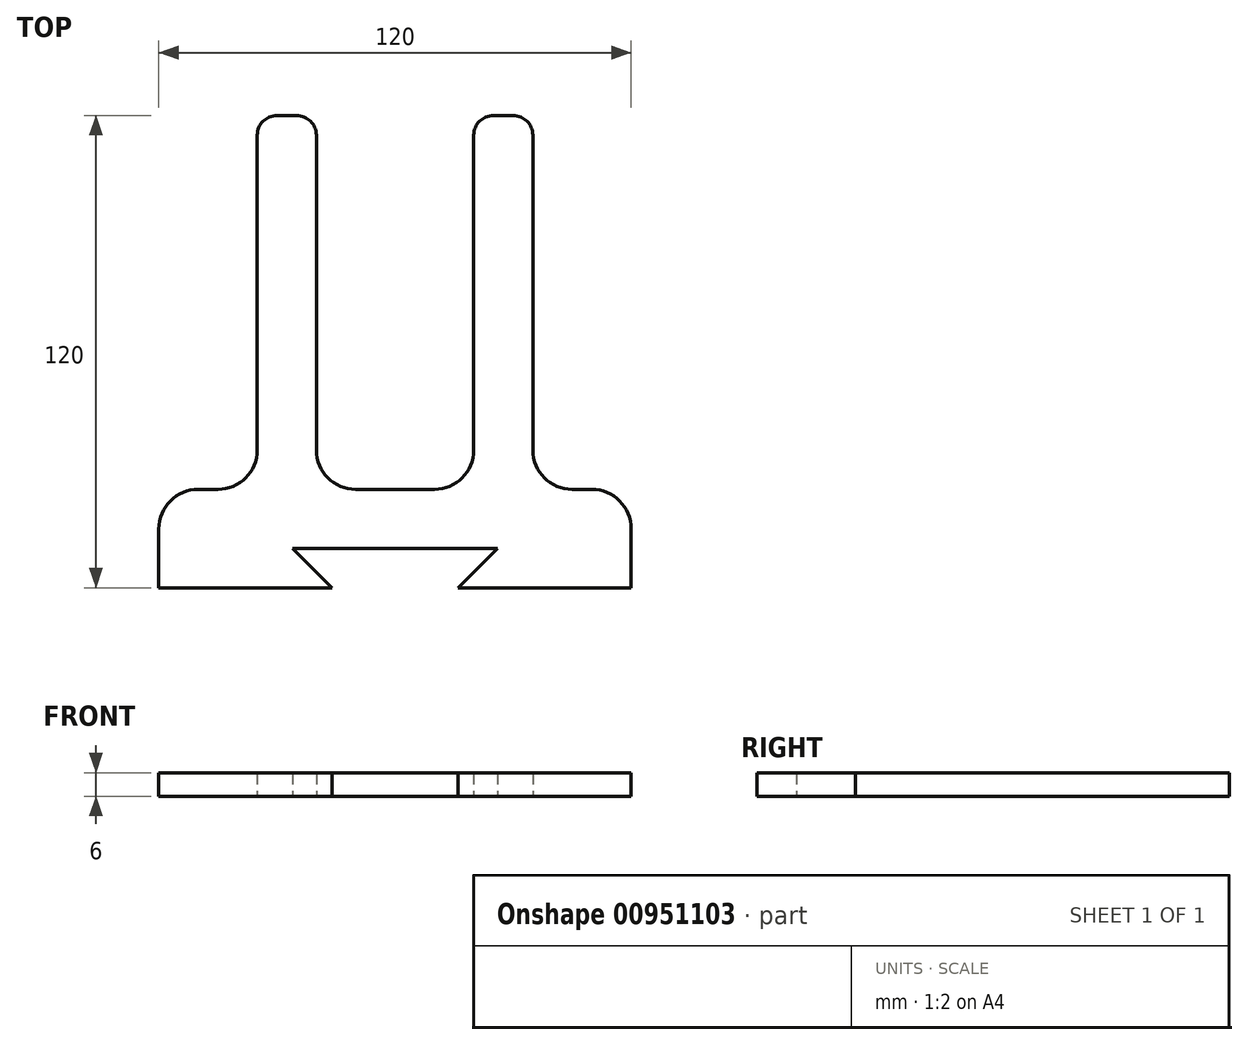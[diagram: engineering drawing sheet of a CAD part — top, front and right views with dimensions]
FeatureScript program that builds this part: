
annotation { "Feature Type Name" : "Feature", "Feature Type Description" : "" }
export const myFeature = defineFeature(function(context is Context, id is Id, definition is map)
    precondition{}
    {
        {
            var Q0;
            Q0=qCreatedBy(makeId("Top.planeOp"),FACE);
            var sketch = newSketch(context, id + "F0", { "sketchPlane" : qUnion([Q0])});
            skLineSegment(sketch, "E0", {"start": v(80, -30.9) * mm, "end": v(80, -15.9) * mm});
            skLineSegment(sketch, "E1", {"start": v(70, -5.9) * mm, "end": v(65, -5.9) * mm});
            skLineSegment(sketch, "E2", {"start": v(55, 4.1) * mm, "end": v(55, 84.1) * mm});
            skLineSegment(sketch, "E3", {"start": v(50, 89.1) * mm, "end": v(45, 89.1) * mm});
            skLineSegment(sketch, "E4", {"start": v(40, 84.1) * mm, "end": v(40, 4.1) * mm});
            skLineSegment(sketch, "E5", {"start": v(30, -5.9) * mm, "end": v(10, -5.9) * mm});
            skLineSegment(sketch, "E6", {"start": v(0, 4.1) * mm, "end": v(0, 84.1) * mm});
            skLineSegment(sketch, "E7", {"start": v(-5, 89.1) * mm, "end": v(-10, 89.1) * mm});
            skLineSegment(sketch, "E8", {"start": v(-15, 84.1) * mm, "end": v(-15, 4.1) * mm});
            skLineSegment(sketch, "E9", {"start": v(-25, -5.9) * mm, "end": v(-30, -5.9) * mm});
            skLineSegment(sketch, "E10", {"start": v(-40, -15.9) * mm, "end": v(-40, -30.9) * mm});
            skPoint(sketch, "E11.visualSharp", {"position": v(55, -5.9) * mm});
            skArc(sketch, "E11.filletArc", {"start": v(55, 4.1) * mm, "mid": v(57.93, -2.97) * mm, "end": v(65, -5.9) * mm});
            skPoint(sketch, "E12.visualSharp", {"position": v(40, -5.9) * mm});
            skArc(sketch, "E12.filletArc", {"start": v(30, -5.9) * mm, "mid": v(37.07, -2.97) * mm, "end": v(40, 4.1) * mm});
            skPoint(sketch, "E13.visualSharp", {"position": v(0, -5.9) * mm});
            skArc(sketch, "E13.filletArc", {"start": v(0, 4.1) * mm, "mid": v(2.93, -2.97) * mm, "end": v(10, -5.9) * mm});
            skPoint(sketch, "E14.visualSharp", {"position": v(-15, -5.9) * mm});
            skArc(sketch, "E14.filletArc", {"start": v(-25, -5.9) * mm, "mid": v(-17.93, -2.97) * mm, "end": v(-15, 4.1) * mm});
            skPoint(sketch, "E15.visualSharp", {"position": v(-40, -5.9) * mm});
            skArc(sketch, "E15.filletArc", {"start": v(-30, -5.9) * mm, "mid": v(-37.07, -8.82) * mm, "end": v(-40, -15.9) * mm});
            skPoint(sketch, "E16.visualSharp", {"position": v(80, -5.9) * mm});
            skArc(sketch, "E16.filletArc", {"start": v(80, -15.9) * mm, "mid": v(77.07, -8.82) * mm, "end": v(70, -5.9) * mm});
            skPoint(sketch, "E17.visualSharp", {"position": v(55, 89.1) * mm});
            skArc(sketch, "E17.filletArc", {"start": v(55, 84.1) * mm, "mid": v(53.54, 87.64) * mm, "end": v(50, 89.1) * mm});
            skPoint(sketch, "E18.visualSharp", {"position": v(40, 89.1) * mm});
            skArc(sketch, "E18.filletArc", {"start": v(45, 89.1) * mm, "mid": v(41.46, 87.64) * mm, "end": v(40, 84.1) * mm});
            skPoint(sketch, "E19.visualSharp", {"position": v(0, 89.1) * mm});
            skArc(sketch, "E19.filletArc", {"start": v(0, 84.1) * mm, "mid": v(-1.46, 87.64) * mm, "end": v(-5, 89.1) * mm});
            skPoint(sketch, "E20.visualSharp", {"position": v(-15, 89.1) * mm});
            skArc(sketch, "E20.filletArc", {"start": v(-10, 89.1) * mm, "mid": v(-13.54, 87.64) * mm, "end": v(-15, 84.1) * mm});
            skPoint(sketch, "E21.center.orphan", {"position": v(-27.5, -18.4) * mm});
            skPoint(sketch, "E22.end.orphan", {"position": v(0, -30.9) * mm});
            skLineSegment(sketch, "E23", {"start": v(-40, -30.9) * mm, "end": v(4, -30.9) * mm});
            skLineSegment(sketch, "E24", {"start": v(80, -30.9) * mm, "end": v(36, -30.9) * mm});
            skLineSegment(sketch, "E25", {"start": v(36, -30.9) * mm, "end": v(46, -20.9) * mm});
            skLineSegment(sketch, "E26", {"start": v(4, -30.9) * mm, "end": v(-6, -20.9) * mm});
            skLineSegment(sketch, "E27", {"start": v(20, -20.9) * mm, "end": v(-6, -20.9) * mm});
            skLineSegment(sketch, "E28", {"start": v(-6, -20.9) * mm, "end": v(46, -20.9) * mm});
            skPoint(sketch, "E29.start.orphan", {"position": v(20, -30.9) * mm});
            skPoint(sketch, "E30.center.orphan", {"position": v(67.5, -18.4) * mm});
            skSolve(sketch);
        }
        {
            var Q0;
            Q0=makeQuery(id+"F0.imprint","IMPRINT",FACE,{"disambiguationData":[TD([[makeQuery(id+"F0.imprint","IMPRINT",EDGE,{"derivedFrom":sQuery(id+"F0.wireOp",EDGE,"E0")}),1.0]])]});
            extrude(context, id + "F1", {"entities" : qUnion([Q0]), "depth" : 6 * mm, "offsetDistance" : 25 * mm});
        }
    });
